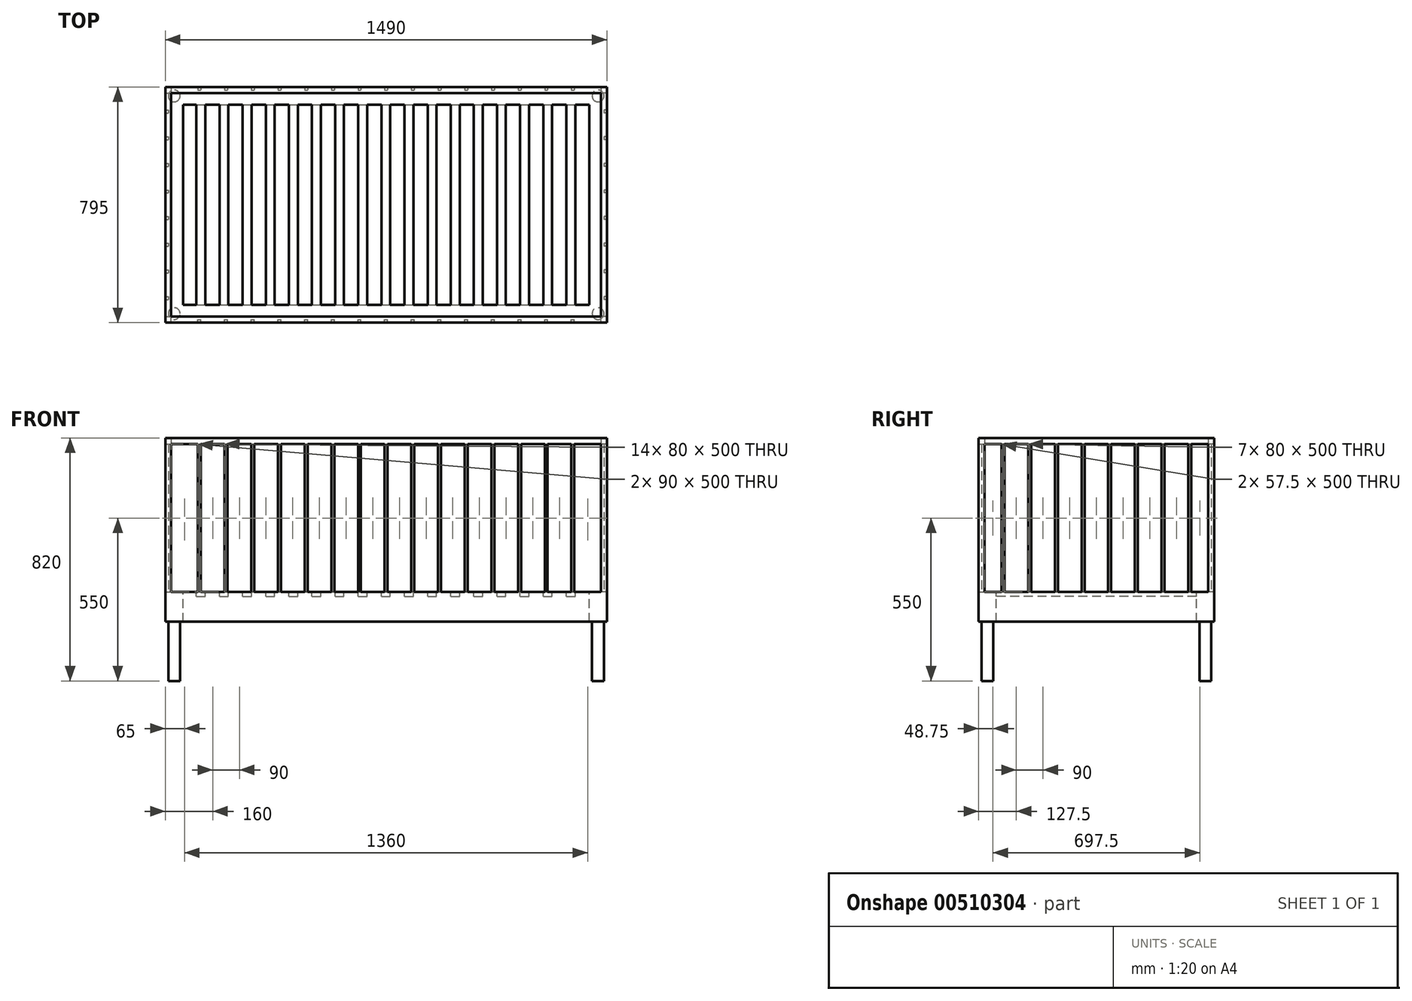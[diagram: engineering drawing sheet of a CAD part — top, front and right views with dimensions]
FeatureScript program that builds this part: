
annotation { "Feature Type Name" : "Feature", "Feature Type Description" : "" }
export const myFeature = defineFeature(function(context is Context, id is Id, definition is map)
    precondition{}
    {
        {
            var Q0;
            Q0=qCreatedBy(makeId("Top.planeOp"),FACE);
            var sketch = newSketch(context, id + "F0", { "sketchPlane" : qUnion([Q0])});
            skLineSegment(sketch, "E0.bottom", {"start": v(-745, 397.5) * mm, "end": v(745, 397.5) * mm});
            skLineSegment(sketch, "E0.top", {"start": v(-745, -397.5) * mm, "end": v(745, -397.5) * mm});
            skLineSegment(sketch, "E0.left", {"start": v(-745, 397.5) * mm, "end": v(-745, -397.5) * mm});
            skLineSegment(sketch, "E0.right", {"start": v(745, 397.5) * mm, "end": v(745, -397.5) * mm});
            skPoint(sketch, "E0.middle", {"position": v(0, 0) * mm});
            skLineSegment(sketch, "E1.bottom", {"start": v(-685, 337.5) * mm, "end": v(685, 337.5) * mm});
            skLineSegment(sketch, "E1.top", {"start": v(-685, -337.5) * mm, "end": v(685, -337.5) * mm});
            skLineSegment(sketch, "E1.left", {"start": v(-685, 337.5) * mm, "end": v(-685, -337.5) * mm});
            skLineSegment(sketch, "E1.right", {"start": v(685, 337.5) * mm, "end": v(685, -337.5) * mm});
            skLineSegment(sketch, "E2", {"start": v(-640, 337.5) * mm, "end": v(-640, -337.5) * mm});
            skLineSegment(sketch, "E3", {"start": v(-640, -337.5) * mm, "end": v(-610, -337.5) * mm});
            skLineSegment(sketch, "E4", {"start": v(-610, -337.5) * mm, "end": v(-610, 337.5) * mm});
            skLineSegment(sketch, "E5.1.0.0", {"start": v(-532, -337.5) * mm, "end": v(-532, 337.5) * mm});
            skLineSegment(sketch, "E5.1.0.1", {"start": v(-562, 337.5) * mm, "end": v(-562, -337.5) * mm});
            skLineSegment(sketch, "E5.2.0.0", {"start": v(-454, -337.5) * mm, "end": v(-454, 337.5) * mm});
            skLineSegment(sketch, "E5.2.0.1", {"start": v(-484, 337.5) * mm, "end": v(-484, -337.5) * mm});
            skLineSegment(sketch, "E5.3.0.0", {"start": v(-376, -337.5) * mm, "end": v(-376, 337.5) * mm});
            skLineSegment(sketch, "E5.3.0.1", {"start": v(-406, 337.5) * mm, "end": v(-406, -337.5) * mm});
            skLineSegment(sketch, "E5.4.0.0", {"start": v(-298, -337.5) * mm, "end": v(-298, 337.5) * mm});
            skLineSegment(sketch, "E5.4.0.1", {"start": v(-328, 337.5) * mm, "end": v(-328, -337.5) * mm});
            skLineSegment(sketch, "E5.5.0.0", {"start": v(-220, -337.5) * mm, "end": v(-220, 337.5) * mm});
            skLineSegment(sketch, "E5.5.0.1", {"start": v(-250, 337.5) * mm, "end": v(-250, -337.5) * mm});
            skLineSegment(sketch, "E5.6.0.0", {"start": v(-142, -337.5) * mm, "end": v(-142, 337.5) * mm});
            skLineSegment(sketch, "E5.6.0.1", {"start": v(-172, 337.5) * mm, "end": v(-172, -337.5) * mm});
            skLineSegment(sketch, "E5.7.0.0", {"start": v(-64, -337.5) * mm, "end": v(-64, 337.5) * mm});
            skLineSegment(sketch, "E5.7.0.1", {"start": v(-94, 337.5) * mm, "end": v(-94, -337.5) * mm});
            skLineSegment(sketch, "E5.8.0.0", {"start": v(14, -337.5) * mm, "end": v(14, 337.5) * mm});
            skLineSegment(sketch, "E5.8.0.1", {"start": v(-16, 337.5) * mm, "end": v(-16, -337.5) * mm});
            skLineSegment(sketch, "E5.9.0.0", {"start": v(92, -337.5) * mm, "end": v(92, 337.5) * mm});
            skLineSegment(sketch, "E5.9.0.1", {"start": v(62, 337.5) * mm, "end": v(62, -337.5) * mm});
            skLineSegment(sketch, "E5.10.0.0", {"start": v(170, -337.5) * mm, "end": v(170, 337.5) * mm});
            skLineSegment(sketch, "E5.10.0.1", {"start": v(140, 337.5) * mm, "end": v(140, -337.5) * mm});
            skLineSegment(sketch, "E5.11.0.0", {"start": v(248, -337.5) * mm, "end": v(248, 337.5) * mm});
            skLineSegment(sketch, "E5.11.0.1", {"start": v(218, 337.5) * mm, "end": v(218, -337.5) * mm});
            skLineSegment(sketch, "E5.12.0.0", {"start": v(326, -337.5) * mm, "end": v(326, 337.5) * mm});
            skLineSegment(sketch, "E5.12.0.1", {"start": v(296, 337.5) * mm, "end": v(296, -337.5) * mm});
            skLineSegment(sketch, "E5.13.0.0", {"start": v(404, -337.5) * mm, "end": v(404, 337.5) * mm});
            skLineSegment(sketch, "E5.13.0.1", {"start": v(374, 337.5) * mm, "end": v(374, -337.5) * mm});
            skLineSegment(sketch, "E5.14.0.0", {"start": v(482, -337.5) * mm, "end": v(482, 337.5) * mm});
            skLineSegment(sketch, "E5.14.0.1", {"start": v(452, 337.5) * mm, "end": v(452, -337.5) * mm});
            skLineSegment(sketch, "E5.15.0.0", {"start": v(560, -337.5) * mm, "end": v(560, 337.5) * mm});
            skLineSegment(sketch, "E5.15.0.1", {"start": v(530, 337.5) * mm, "end": v(530, -337.5) * mm});
            skLineSegment(sketch, "E5.16.0.0", {"start": v(638, -337.5) * mm, "end": v(638, 337.5) * mm});
            skLineSegment(sketch, "E5.16.0.1", {"start": v(608, 337.5) * mm, "end": v(608, -337.5) * mm});
            skLineSegment(sketch, "E5.direction1", {"start": v(-610, -337.5) * mm, "end": v(-532, -337.5) * mm, "construction": true});
            skSolve(sketch);
        }
        {
            var Q0;
            Q0=makeQuery(id+"F0.imprint","IMPRINT",FACE,{"disambiguationData":[TD([[makeQuery(id+"F0.imprint","IMPRINT",EDGE,{"derivedFrom":sQuery(id+"F0.wireOp",EDGE,"E0.bottom")}),-1.0]])]});
            var Q1;
            {var subQ0=sQuery(id+"F0.wireOp",EDGE,"E2");Q1=makeQuery(id+"F0.imprint","IMPRINT",FACE,{"disambiguationData":[TD([[makeQuery(id+"F0.imprint","IMPRINT",EDGE,{"derivedFrom":subQ0}),1.0]])]});}
            var Q2;
            {var subQ0=sQuery(id+"F0.wireOp",EDGE,"E5.1.0.0");Q2=makeQuery(id+"F0.imprint","IMPRINT",FACE,{"disambiguationData":[TD([[makeQuery(id+"F0.imprint","IMPRINT",EDGE,{"derivedFrom":subQ0}),1.0]])]});}
            var Q3;
            {var subQ0=sQuery(id+"F0.wireOp",EDGE,"E5.2.0.0");Q3=makeQuery(id+"F0.imprint","IMPRINT",FACE,{"disambiguationData":[TD([[makeQuery(id+"F0.imprint","IMPRINT",EDGE,{"derivedFrom":subQ0}),1.0]])]});}
            var Q4;
            {var subQ0=sQuery(id+"F0.wireOp",EDGE,"E5.3.0.0");Q4=makeQuery(id+"F0.imprint","IMPRINT",FACE,{"disambiguationData":[TD([[makeQuery(id+"F0.imprint","IMPRINT",EDGE,{"derivedFrom":subQ0}),1.0]])]});}
            var Q5;
            {var subQ0=sQuery(id+"F0.wireOp",EDGE,"E5.4.0.0");Q5=makeQuery(id+"F0.imprint","IMPRINT",FACE,{"disambiguationData":[TD([[makeQuery(id+"F0.imprint","IMPRINT",EDGE,{"derivedFrom":subQ0}),1.0]])]});}
            var Q6;
            {var subQ0=sQuery(id+"F0.wireOp",EDGE,"E5.5.0.0");Q6=makeQuery(id+"F0.imprint","IMPRINT",FACE,{"disambiguationData":[TD([[makeQuery(id+"F0.imprint","IMPRINT",EDGE,{"derivedFrom":subQ0}),1.0]])]});}
            var Q7;
            {var subQ0=sQuery(id+"F0.wireOp",EDGE,"E5.6.0.0");Q7=makeQuery(id+"F0.imprint","IMPRINT",FACE,{"disambiguationData":[TD([[makeQuery(id+"F0.imprint","IMPRINT",EDGE,{"derivedFrom":subQ0}),1.0]])]});}
            var Q8;
            {var subQ0=sQuery(id+"F0.wireOp",EDGE,"E5.7.0.0");Q8=makeQuery(id+"F0.imprint","IMPRINT",FACE,{"disambiguationData":[TD([[makeQuery(id+"F0.imprint","IMPRINT",EDGE,{"derivedFrom":subQ0}),1.0]])]});}
            var Q9;
            {var subQ0=sQuery(id+"F0.wireOp",EDGE,"E5.8.0.0");Q9=makeQuery(id+"F0.imprint","IMPRINT",FACE,{"disambiguationData":[TD([[makeQuery(id+"F0.imprint","IMPRINT",EDGE,{"derivedFrom":subQ0}),1.0]])]});}
            var Q10;
            {var subQ0=sQuery(id+"F0.wireOp",EDGE,"E5.9.0.0");Q10=makeQuery(id+"F0.imprint","IMPRINT",FACE,{"disambiguationData":[TD([[makeQuery(id+"F0.imprint","IMPRINT",EDGE,{"derivedFrom":subQ0}),1.0]])]});}
            var Q11;
            {var subQ0=sQuery(id+"F0.wireOp",EDGE,"E5.10.0.0");Q11=makeQuery(id+"F0.imprint","IMPRINT",FACE,{"disambiguationData":[TD([[makeQuery(id+"F0.imprint","IMPRINT",EDGE,{"derivedFrom":subQ0}),1.0]])]});}
            var Q12;
            {var subQ0=sQuery(id+"F0.wireOp",EDGE,"E5.11.0.0");Q12=makeQuery(id+"F0.imprint","IMPRINT",FACE,{"disambiguationData":[TD([[makeQuery(id+"F0.imprint","IMPRINT",EDGE,{"derivedFrom":subQ0}),1.0]])]});}
            var Q13;
            {var subQ0=sQuery(id+"F0.wireOp",EDGE,"E5.12.0.0");Q13=makeQuery(id+"F0.imprint","IMPRINT",FACE,{"disambiguationData":[TD([[makeQuery(id+"F0.imprint","IMPRINT",EDGE,{"derivedFrom":subQ0}),1.0]])]});}
            var Q14;
            {var subQ0=sQuery(id+"F0.wireOp",EDGE,"E5.13.0.0");Q14=makeQuery(id+"F0.imprint","IMPRINT",FACE,{"disambiguationData":[TD([[makeQuery(id+"F0.imprint","IMPRINT",EDGE,{"derivedFrom":subQ0}),1.0]])]});}
            var Q15;
            {var subQ0=sQuery(id+"F0.wireOp",EDGE,"E5.14.0.0");Q15=makeQuery(id+"F0.imprint","IMPRINT",FACE,{"disambiguationData":[TD([[makeQuery(id+"F0.imprint","IMPRINT",EDGE,{"derivedFrom":subQ0}),1.0]])]});}
            var Q16;
            {var subQ0=sQuery(id+"F0.wireOp",EDGE,"E5.15.0.0");Q16=makeQuery(id+"F0.imprint","IMPRINT",FACE,{"disambiguationData":[TD([[makeQuery(id+"F0.imprint","IMPRINT",EDGE,{"derivedFrom":subQ0}),1.0]])]});}
            var Q17;
            {var subQ0=sQuery(id+"F0.wireOp",EDGE,"E5.16.0.0");Q17=makeQuery(id+"F0.imprint","IMPRINT",FACE,{"disambiguationData":[TD([[makeQuery(id+"F0.imprint","IMPRINT",EDGE,{"derivedFrom":subQ0}),1.0]])]});}
            var Q18;
            {var subQ0=sQuery(id+"F0.wireOp",EDGE,"E5.17.0.0");Q18=makeQuery(id+"F0.imprint","IMPRINT",FACE,{"disambiguationData":[TD([[makeQuery(id+"F0.imprint","IMPRINT",EDGE,{"derivedFrom":subQ0}),1.0]])]});}
            var Q19;
            {var subQ0=sQuery(id+"F0.wireOp",EDGE,"E5.18.0.0");Q19=makeQuery(id+"F0.imprint","IMPRINT",FACE,{"disambiguationData":[TD([[makeQuery(id+"F0.imprint","IMPRINT",EDGE,{"derivedFrom":subQ0}),1.0]])]});}
            var Q20;
            {var subQ0=sQuery(id+"F0.wireOp",EDGE,"E5.19.0.0");Q20=makeQuery(id+"F0.imprint","IMPRINT",FACE,{"disambiguationData":[TD([[makeQuery(id+"F0.imprint","IMPRINT",EDGE,{"derivedFrom":subQ0}),1.0]])]});}
            var Q21;
            {var subQ0=sQuery(id+"F0.wireOp",EDGE,"E5.20.0.0");Q21=makeQuery(id+"F0.imprint","IMPRINT",FACE,{"disambiguationData":[TD([[makeQuery(id+"F0.imprint","IMPRINT",EDGE,{"derivedFrom":subQ0}),1.0]])]});}
            var Q22;
            {var subQ0=sQuery(id+"F0.wireOp",EDGE,"E5.21.0.0");Q22=makeQuery(id+"F0.imprint","IMPRINT",FACE,{"disambiguationData":[TD([[makeQuery(id+"F0.imprint","IMPRINT",EDGE,{"derivedFrom":subQ0}),1.0]])]});}
            var Q23;
            {var subQ0=sQuery(id+"F0.wireOp",EDGE,"E5.22.0.0");Q23=makeQuery(id+"F0.imprint","IMPRINT",FACE,{"disambiguationData":[TD([[makeQuery(id+"F0.imprint","IMPRINT",EDGE,{"derivedFrom":subQ0}),1.0]])]});}
            extrude(context, id + "F1", {"entities" : qUnion([Q0, Q1, Q2, Q3, Q4, Q5, Q6, Q7, Q8, Q9, Q10, Q11, Q12, Q13, Q14, Q15, Q16, Q17, Q18, Q19, Q20, Q21, Q22, Q23]), "oppositeDirection" : true, "depth" : 15 * mm});
        }
        {
            var Q0;
            Q0=qSketchRegion(id+"F0",true);
            extrude(context, id + "F2", {"entities" : qUnion([Q0]), "operationType" : NewBodyOperationType.ADD, "oppositeDirection" : true, "depth" : 100 * mm});
        }
        {
            var Q0;
            Q0=makeQuery(id+"F2.opExtrude","CAP_FACE",FACE,{"disambiguationData":[OSD([sQuery(id+"F0.wireOp",EDGE,"E0.bottom"),sQuery(id+"F0.wireOp",EDGE,"E0.top"),sQuery(id+"F0.wireOp",EDGE,"E0.left"),sQuery(id+"F0.wireOp",EDGE,"E0.right"),sQuery(id+"F0.wireOp",EDGE,"E1.bottom"),sQuery(id+"F0.wireOp",EDGE,"E1.top"),sQuery(id+"F0.wireOp",EDGE,"E1.left"),sQuery(id+"F0.wireOp",EDGE,"E1.right"),sQuery(id+"F0.wireOp",EDGE,"E3")])],"isStart":false});
            var sketch = newSketch(context, id + "F3", { "sketchPlane" : qUnion([Q0])});
            skCircle(sketch, "E6", {"center": v(-715, 367.5) * mm, "radius": 20 * mm});
            skCircle(sketch, "E7", {"center": v(715, 367.5) * mm, "radius": 20 * mm});
            skCircle(sketch, "E8", {"center": v(715, -367.5) * mm, "radius": 20 * mm});
            skCircle(sketch, "E9", {"center": v(-715, -367.5) * mm, "radius": 20 * mm});
            skSolve(sketch);
        }
        {
            var Q0;
            Q0=qSketchRegion(id+"F3",true);
            extrude(context, id + "F4", {"entities" : qUnion([Q0]), "operationType" : NewBodyOperationType.ADD, "depth" : 200 * mm});
        }
        {
            var Q0;
            Q0=makeQuery(id+"F1.opExtrude","CAP_FACE",FACE,{"disambiguationData":[OSD([sQuery(id+"F0.wireOp",EDGE,"E0.bottom"),sQuery(id+"F0.wireOp",EDGE,"E0.top"),sQuery(id+"F0.wireOp",EDGE,"E0.left"),sQuery(id+"F0.wireOp",EDGE,"E0.right"),sQuery(id+"F0.wireOp",EDGE,"E1.bottom"),sQuery(id+"F0.wireOp",EDGE,"E1.top"),sQuery(id+"F0.wireOp",EDGE,"E1.left"),sQuery(id+"F0.wireOp",EDGE,"E1.right"),sQuery(id+"F0.wireOp",EDGE,"E2"),sQuery(id+"F0.wireOp",EDGE,"E4"),sQuery(id+"F0.wireOp",EDGE,"E5.1.0.0"),sQuery(id+"F0.wireOp",EDGE,"E5.1.0.1"),sQuery(id+"F0.wireOp",EDGE,"E5.2.0.0"),sQuery(id+"F0.wireOp",EDGE,"E5.2.0.1"),sQuery(id+"F0.wireOp",EDGE,"E5.3.0.0"),sQuery(id+"F0.wireOp",EDGE,"E5.3.0.1"),sQuery(id+"F0.wireOp",EDGE,"E5.4.0.0"),sQuery(id+"F0.wireOp",EDGE,"E5.4.0.1"),sQuery(id+"F0.wireOp",EDGE,"E5.5.0.0"),sQuery(id+"F0.wireOp",EDGE,"E5.5.0.1"),sQuery(id+"F0.wireOp",EDGE,"E5.6.0.0"),sQuery(id+"F0.wireOp",EDGE,"E5.6.0.1"),sQuery(id+"F0.wireOp",EDGE,"E5.7.0.0"),sQuery(id+"F0.wireOp",EDGE,"E5.7.0.1"),sQuery(id+"F0.wireOp",EDGE,"E5.8.0.0"),sQuery(id+"F0.wireOp",EDGE,"E5.8.0.1"),sQuery(id+"F0.wireOp",EDGE,"E5.9.0.0"),sQuery(id+"F0.wireOp",EDGE,"E5.9.0.1"),sQuery(id+"F0.wireOp",EDGE,"E5.10.0.0"),sQuery(id+"F0.wireOp",EDGE,"E5.10.0.1"),sQuery(id+"F0.wireOp",EDGE,"E5.11.0.0"),sQuery(id+"F0.wireOp",EDGE,"E5.11.0.1"),sQuery(id+"F0.wireOp",EDGE,"E5.12.0.0"),sQuery(id+"F0.wireOp",EDGE,"E5.12.0.1"),sQuery(id+"F0.wireOp",EDGE,"E5.13.0.0"),sQuery(id+"F0.wireOp",EDGE,"E5.13.0.1"),sQuery(id+"F0.wireOp",EDGE,"E5.14.0.0"),sQuery(id+"F0.wireOp",EDGE,"E5.14.0.1"),sQuery(id+"F0.wireOp",EDGE,"E5.15.0.0"),sQuery(id+"F0.wireOp",EDGE,"E5.15.0.1"),sQuery(id+"F0.wireOp",EDGE,"E5.16.0.0"),sQuery(id+"F0.wireOp",EDGE,"E5.16.0.1")])],"isStart":true});
            var sketch = newSketch(context, id + "F5", { "sketchPlane" : qUnion([Q0])});
            skLineSegment(sketch, "E10.bottom", {"start": v(-745, 397.5) * mm, "end": v(-725, 397.5) * mm});
            skLineSegment(sketch, "E10.top", {"start": v(-745, 377.5) * mm, "end": v(-725, 377.5) * mm});
            skLineSegment(sketch, "E10.left", {"start": v(-745, 397.5) * mm, "end": v(-745, 377.5) * mm});
            skLineSegment(sketch, "E10.right", {"start": v(-725, 397.5) * mm, "end": v(-725, 377.5) * mm});
            skLineSegment(sketch, "E11.bottom", {"start": v(745, 397.5) * mm, "end": v(725, 397.5) * mm});
            skLineSegment(sketch, "E11.top", {"start": v(745, 377.5) * mm, "end": v(725, 377.5) * mm});
            skLineSegment(sketch, "E11.left", {"start": v(745, 397.5) * mm, "end": v(745, 377.5) * mm});
            skLineSegment(sketch, "E11.right", {"start": v(725, 397.5) * mm, "end": v(725, 377.5) * mm});
            skLineSegment(sketch, "E12.bottom", {"start": v(-635, 397.5) * mm, "end": v(-625, 397.5) * mm});
            skLineSegment(sketch, "E12.top", {"start": v(-635, 387.5) * mm, "end": v(-625, 387.5) * mm});
            skLineSegment(sketch, "E12.left", {"start": v(-635, 397.5) * mm, "end": v(-635, 387.5) * mm});
            skLineSegment(sketch, "E12.right", {"start": v(-625, 397.5) * mm, "end": v(-625, 387.5) * mm});
            skLineSegment(sketch, "E13.1.0.0", {"start": v(-545, 387.5) * mm, "end": v(-535, 387.5) * mm});
            skLineSegment(sketch, "E13.1.0.1", {"start": v(-545, 397.5) * mm, "end": v(-535, 397.5) * mm});
            skLineSegment(sketch, "E13.1.0.2", {"start": v(-535, 397.5) * mm, "end": v(-535, 387.5) * mm});
            skLineSegment(sketch, "E13.1.0.3", {"start": v(-545, 397.5) * mm, "end": v(-545, 387.5) * mm});
            skLineSegment(sketch, "E13.2.0.0", {"start": v(-455, 387.5) * mm, "end": v(-445, 387.5) * mm});
            skLineSegment(sketch, "E13.2.0.1", {"start": v(-455, 397.5) * mm, "end": v(-445, 397.5) * mm});
            skLineSegment(sketch, "E13.2.0.2", {"start": v(-445, 397.5) * mm, "end": v(-445, 387.5) * mm});
            skLineSegment(sketch, "E13.2.0.3", {"start": v(-455, 397.5) * mm, "end": v(-455, 387.5) * mm});
            skLineSegment(sketch, "E13.3.0.0", {"start": v(-365, 387.5) * mm, "end": v(-355, 387.5) * mm});
            skLineSegment(sketch, "E13.3.0.1", {"start": v(-365, 397.5) * mm, "end": v(-355, 397.5) * mm});
            skLineSegment(sketch, "E13.3.0.2", {"start": v(-355, 397.5) * mm, "end": v(-355, 387.5) * mm});
            skLineSegment(sketch, "E13.3.0.3", {"start": v(-365, 397.5) * mm, "end": v(-365, 387.5) * mm});
            skLineSegment(sketch, "E13.4.0.0", {"start": v(-275, 387.5) * mm, "end": v(-265, 387.5) * mm});
            skLineSegment(sketch, "E13.4.0.1", {"start": v(-275, 397.5) * mm, "end": v(-265, 397.5) * mm});
            skLineSegment(sketch, "E13.4.0.2", {"start": v(-265, 397.5) * mm, "end": v(-265, 387.5) * mm});
            skLineSegment(sketch, "E13.4.0.3", {"start": v(-275, 397.5) * mm, "end": v(-275, 387.5) * mm});
            skLineSegment(sketch, "E13.5.0.0", {"start": v(-185, 387.5) * mm, "end": v(-175, 387.5) * mm});
            skLineSegment(sketch, "E13.5.0.1", {"start": v(-185, 397.5) * mm, "end": v(-175, 397.5) * mm});
            skLineSegment(sketch, "E13.5.0.2", {"start": v(-175, 397.5) * mm, "end": v(-175, 387.5) * mm});
            skLineSegment(sketch, "E13.5.0.3", {"start": v(-185, 397.5) * mm, "end": v(-185, 387.5) * mm});
            skLineSegment(sketch, "E13.6.0.0", {"start": v(-95, 387.5) * mm, "end": v(-85, 387.5) * mm});
            skLineSegment(sketch, "E13.6.0.1", {"start": v(-95, 397.5) * mm, "end": v(-85, 397.5) * mm});
            skLineSegment(sketch, "E13.6.0.2", {"start": v(-85, 397.5) * mm, "end": v(-85, 387.5) * mm});
            skLineSegment(sketch, "E13.6.0.3", {"start": v(-95, 397.5) * mm, "end": v(-95, 387.5) * mm});
            skLineSegment(sketch, "E13.7.0.0", {"start": v(-5, 387.5) * mm, "end": v(5, 387.5) * mm});
            skLineSegment(sketch, "E13.7.0.1", {"start": v(-5, 397.5) * mm, "end": v(5, 397.5) * mm});
            skLineSegment(sketch, "E13.7.0.2", {"start": v(5, 397.5) * mm, "end": v(5, 387.5) * mm});
            skLineSegment(sketch, "E13.7.0.3", {"start": v(-5, 397.5) * mm, "end": v(-5, 387.5) * mm});
            skLineSegment(sketch, "E13.8.0.0", {"start": v(85, 387.5) * mm, "end": v(95, 387.5) * mm});
            skLineSegment(sketch, "E13.8.0.1", {"start": v(85, 397.5) * mm, "end": v(95, 397.5) * mm});
            skLineSegment(sketch, "E13.8.0.2", {"start": v(95, 397.5) * mm, "end": v(95, 387.5) * mm});
            skLineSegment(sketch, "E13.8.0.3", {"start": v(85, 397.5) * mm, "end": v(85, 387.5) * mm});
            skLineSegment(sketch, "E13.9.0.0", {"start": v(175, 387.5) * mm, "end": v(185, 387.5) * mm});
            skLineSegment(sketch, "E13.9.0.1", {"start": v(175, 397.5) * mm, "end": v(185, 397.5) * mm});
            skLineSegment(sketch, "E13.9.0.2", {"start": v(185, 397.5) * mm, "end": v(185, 387.5) * mm});
            skLineSegment(sketch, "E13.9.0.3", {"start": v(175, 397.5) * mm, "end": v(175, 387.5) * mm});
            skLineSegment(sketch, "E13.10.0.0", {"start": v(265, 387.5) * mm, "end": v(275, 387.5) * mm});
            skLineSegment(sketch, "E13.10.0.1", {"start": v(265, 397.5) * mm, "end": v(275, 397.5) * mm});
            skLineSegment(sketch, "E13.10.0.2", {"start": v(275, 397.5) * mm, "end": v(275, 387.5) * mm});
            skLineSegment(sketch, "E13.10.0.3", {"start": v(265, 397.5) * mm, "end": v(265, 387.5) * mm});
            skLineSegment(sketch, "E13.11.0.0", {"start": v(355, 387.5) * mm, "end": v(365, 387.5) * mm});
            skLineSegment(sketch, "E13.11.0.1", {"start": v(355, 397.5) * mm, "end": v(365, 397.5) * mm});
            skLineSegment(sketch, "E13.11.0.2", {"start": v(365, 397.5) * mm, "end": v(365, 387.5) * mm});
            skLineSegment(sketch, "E13.11.0.3", {"start": v(355, 397.5) * mm, "end": v(355, 387.5) * mm});
            skLineSegment(sketch, "E13.12.0.0", {"start": v(445, 387.5) * mm, "end": v(455, 387.5) * mm});
            skLineSegment(sketch, "E13.12.0.1", {"start": v(445, 397.5) * mm, "end": v(455, 397.5) * mm});
            skLineSegment(sketch, "E13.12.0.2", {"start": v(455, 397.5) * mm, "end": v(455, 387.5) * mm});
            skLineSegment(sketch, "E13.12.0.3", {"start": v(445, 397.5) * mm, "end": v(445, 387.5) * mm});
            skLineSegment(sketch, "E13.13.0.0", {"start": v(535, 387.5) * mm, "end": v(545, 387.5) * mm});
            skLineSegment(sketch, "E13.13.0.1", {"start": v(535, 397.5) * mm, "end": v(545, 397.5) * mm});
            skLineSegment(sketch, "E13.13.0.2", {"start": v(545, 397.5) * mm, "end": v(545, 387.5) * mm});
            skLineSegment(sketch, "E13.13.0.3", {"start": v(535, 397.5) * mm, "end": v(535, 387.5) * mm});
            skLineSegment(sketch, "E13.14.0.0", {"start": v(625, 387.5) * mm, "end": v(635, 387.5) * mm});
            skLineSegment(sketch, "E13.14.0.1", {"start": v(625, 397.5) * mm, "end": v(635, 397.5) * mm});
            skLineSegment(sketch, "E13.14.0.2", {"start": v(635, 397.5) * mm, "end": v(635, 387.5) * mm});
            skLineSegment(sketch, "E13.14.0.3", {"start": v(625, 397.5) * mm, "end": v(625, 387.5) * mm});
            skLineSegment(sketch, "E13.direction1", {"start": v(-635, 387.5) * mm, "end": v(-545, 387.5) * mm, "construction": true});
            skLineSegment(sketch, "E14.MirrorCS", {"start": v(-635, -387.5) * mm, "end": v(-625, -387.5) * mm});
            skLineSegment(sketch, "E15.MirrorCS", {"start": v(-635, -397.5) * mm, "end": v(-625, -397.5) * mm});
            skLineSegment(sketch, "E16.MirrorCS", {"start": v(-545, -397.5) * mm, "end": v(-535, -397.5) * mm});
            skLineSegment(sketch, "E17.MirrorCS", {"start": v(625, -397.5) * mm, "end": v(635, -397.5) * mm});
            skLineSegment(sketch, "E18.MirrorCS", {"start": v(625, -387.5) * mm, "end": v(635, -387.5) * mm});
            skLineSegment(sketch, "E19.MirrorCS", {"start": v(-545, -387.5) * mm, "end": v(-535, -387.5) * mm});
            skLineSegment(sketch, "E20.MirrorCS", {"start": v(-625, -397.5) * mm, "end": v(-625, -387.5) * mm});
            skLineSegment(sketch, "E21.MirrorCS", {"start": v(-635, -397.5) * mm, "end": v(-635, -387.5) * mm});
            skLineSegment(sketch, "E22.MirrorCS", {"start": v(-725, -397.5) * mm, "end": v(-725, -377.5) * mm});
            skLineSegment(sketch, "E23.MirrorCS", {"start": v(-745, -397.5) * mm, "end": v(-725, -397.5) * mm});
            skLineSegment(sketch, "E24.MirrorCS", {"start": v(-545, -397.5) * mm, "end": v(-545, -387.5) * mm});
            skLineSegment(sketch, "E25.MirrorCS", {"start": v(-535, -397.5) * mm, "end": v(-535, -387.5) * mm});
            skLineSegment(sketch, "E26.MirrorCS", {"start": v(85, -397.5) * mm, "end": v(95, -397.5) * mm});
            skLineSegment(sketch, "E27.MirrorCS", {"start": v(535, -397.5) * mm, "end": v(545, -397.5) * mm});
            skLineSegment(sketch, "E28.MirrorCS", {"start": v(-455, -387.5) * mm, "end": v(-445, -387.5) * mm});
            skLineSegment(sketch, "E29.MirrorCS", {"start": v(175, -387.5) * mm, "end": v(185, -387.5) * mm});
            skLineSegment(sketch, "E30.MirrorCS", {"start": v(535, -387.5) * mm, "end": v(545, -387.5) * mm});
            skLineSegment(sketch, "E31.MirrorCS", {"start": v(175, -397.5) * mm, "end": v(185, -397.5) * mm});
            skLineSegment(sketch, "E32.MirrorCS", {"start": v(-455, -397.5) * mm, "end": v(-445, -397.5) * mm});
            skLineSegment(sketch, "E33.MirrorCS", {"start": v(635, -397.5) * mm, "end": v(635, -387.5) * mm});
            skLineSegment(sketch, "E34.MirrorCS", {"start": v(85, -387.5) * mm, "end": v(95, -387.5) * mm});
            skLineSegment(sketch, "E35.MirrorCS", {"start": v(625, -397.5) * mm, "end": v(625, -387.5) * mm});
            skLineSegment(sketch, "E36.MirrorCS", {"start": v(725, -397.5) * mm, "end": v(725, -377.5) * mm});
            skLineSegment(sketch, "E37.MirrorCS", {"start": v(745, -397.5) * mm, "end": v(745, -377.5) * mm});
            skLineSegment(sketch, "E38.MirrorCS", {"start": v(745, -377.5) * mm, "end": v(725, -377.5) * mm});
            skLineSegment(sketch, "E39.MirrorCS", {"start": v(-355, -397.5) * mm, "end": v(-355, -387.5) * mm});
            skLineSegment(sketch, "E40.MirrorCS", {"start": v(5, -397.5) * mm, "end": v(5, -387.5) * mm});
            skLineSegment(sketch, "E41.MirrorCS", {"start": v(-185, -397.5) * mm, "end": v(-185, -387.5) * mm});
            skLineSegment(sketch, "E42.MirrorCS", {"start": v(175, -397.5) * mm, "end": v(175, -387.5) * mm});
            skLineSegment(sketch, "E43.MirrorCS", {"start": v(365, -397.5) * mm, "end": v(365, -387.5) * mm});
            skLineSegment(sketch, "E44.MirrorCS", {"start": v(535, -397.5) * mm, "end": v(535, -387.5) * mm});
            skLineSegment(sketch, "E45.MirrorCS", {"start": v(745, -397.5) * mm, "end": v(725, -397.5) * mm});
            skLineSegment(sketch, "E46.MirrorCS", {"start": v(-745, -397.5) * mm, "end": v(-745, -377.5) * mm});
            skLineSegment(sketch, "E47.MirrorCS", {"start": v(-745, -377.5) * mm, "end": v(-725, -377.5) * mm});
            skLineSegment(sketch, "E48.MirrorCS", {"start": v(-365, -397.5) * mm, "end": v(-365, -387.5) * mm});
            skLineSegment(sketch, "E49.MirrorCS", {"start": v(-275, -397.5) * mm, "end": v(-275, -387.5) * mm});
            skLineSegment(sketch, "E50.MirrorCS", {"start": v(-95, -397.5) * mm, "end": v(-85, -397.5) * mm});
            skLineSegment(sketch, "E51.MirrorCS", {"start": v(355, -397.5) * mm, "end": v(365, -397.5) * mm});
            skLineSegment(sketch, "E52.MirrorCS", {"start": v(-95, -397.5) * mm, "end": v(-95, -387.5) * mm});
            skLineSegment(sketch, "E53.MirrorCS", {"start": v(-365, -397.5) * mm, "end": v(-355, -397.5) * mm});
            skLineSegment(sketch, "E54.MirrorCS", {"start": v(265, -397.5) * mm, "end": v(275, -397.5) * mm});
            skLineSegment(sketch, "E55.MirrorCS", {"start": v(95, -397.5) * mm, "end": v(95, -387.5) * mm});
            skLineSegment(sketch, "E56.MirrorCS", {"start": v(455, -397.5) * mm, "end": v(455, -387.5) * mm});
            skLineSegment(sketch, "E57.MirrorCS", {"start": v(265, -397.5) * mm, "end": v(265, -387.5) * mm});
            skLineSegment(sketch, "E58.MirrorCS", {"start": v(445, -397.5) * mm, "end": v(455, -397.5) * mm});
            skLineSegment(sketch, "E59.MirrorCS", {"start": v(265, -387.5) * mm, "end": v(275, -387.5) * mm});
            skLineSegment(sketch, "E60.MirrorCS", {"start": v(-85, -397.5) * mm, "end": v(-85, -387.5) * mm});
            skLineSegment(sketch, "E61.MirrorCS", {"start": v(355, -387.5) * mm, "end": v(365, -387.5) * mm});
            skLineSegment(sketch, "E62.MirrorCS", {"start": v(275, -397.5) * mm, "end": v(275, -387.5) * mm});
            skLineSegment(sketch, "E63.MirrorCS", {"start": v(355, -397.5) * mm, "end": v(355, -387.5) * mm});
            skLineSegment(sketch, "E64.MirrorCS", {"start": v(-365, -387.5) * mm, "end": v(-355, -387.5) * mm});
            skLineSegment(sketch, "E65.MirrorCS", {"start": v(-5, -387.5) * mm, "end": v(5, -387.5) * mm});
            skLineSegment(sketch, "E66.MirrorCS", {"start": v(-455, -397.5) * mm, "end": v(-455, -387.5) * mm});
            skLineSegment(sketch, "E67.MirrorCS", {"start": v(-445, -397.5) * mm, "end": v(-445, -387.5) * mm});
            skLineSegment(sketch, "E68.MirrorCS", {"start": v(-95, -387.5) * mm, "end": v(-85, -387.5) * mm});
            skLineSegment(sketch, "E69.MirrorCS", {"start": v(445, -397.5) * mm, "end": v(445, -387.5) * mm});
            skLineSegment(sketch, "E70.MirrorCS", {"start": v(-265, -397.5) * mm, "end": v(-265, -387.5) * mm});
            skLineSegment(sketch, "E71.MirrorCS", {"start": v(85, -397.5) * mm, "end": v(85, -387.5) * mm});
            skLineSegment(sketch, "E72.MirrorCS", {"start": v(-185, -397.5) * mm, "end": v(-175, -397.5) * mm});
            skLineSegment(sketch, "E73.MirrorCS", {"start": v(-275, -397.5) * mm, "end": v(-265, -397.5) * mm});
            skLineSegment(sketch, "E74.MirrorCS", {"start": v(-185, -387.5) * mm, "end": v(-175, -387.5) * mm});
            skLineSegment(sketch, "E75.MirrorCS", {"start": v(185, -397.5) * mm, "end": v(185, -387.5) * mm});
            skLineSegment(sketch, "E76.MirrorCS", {"start": v(-5, -397.5) * mm, "end": v(5, -397.5) * mm});
            skLineSegment(sketch, "E77.MirrorCS", {"start": v(545, -397.5) * mm, "end": v(545, -387.5) * mm});
            skLineSegment(sketch, "E78.MirrorCS", {"start": v(-275, -387.5) * mm, "end": v(-265, -387.5) * mm});
            skLineSegment(sketch, "E79.MirrorCS", {"start": v(445, -387.5) * mm, "end": v(455, -387.5) * mm});
            skLineSegment(sketch, "E80.MirrorCS", {"start": v(-175, -397.5) * mm, "end": v(-175, -387.5) * mm});
            skLineSegment(sketch, "E81.MirrorCS", {"start": v(-5, -397.5) * mm, "end": v(-5, -387.5) * mm});
            skLineSegment(sketch, "E82.MirrorCS", {"start": v(-635, -387.5) * mm, "end": v(-545, -387.5) * mm, "construction": true});
            skLineSegment(sketch, "E83.bottom", {"start": v(-745, 320) * mm, "end": v(-735, 320) * mm});
            skLineSegment(sketch, "E83.top", {"start": v(-745, 310) * mm, "end": v(-735, 310) * mm});
            skLineSegment(sketch, "E83.left", {"start": v(-745, 320) * mm, "end": v(-745, 310) * mm});
            skLineSegment(sketch, "E83.right", {"start": v(-735, 320) * mm, "end": v(-735, 310) * mm});
            skLineSegment(sketch, "E84.0.1.0", {"start": v(-745, 220) * mm, "end": v(-735, 220) * mm});
            skLineSegment(sketch, "E84.0.1.1", {"start": v(-745, 230) * mm, "end": v(-745, 220) * mm});
            skLineSegment(sketch, "E84.0.1.2", {"start": v(-745, 230) * mm, "end": v(-735, 230) * mm});
            skLineSegment(sketch, "E84.0.1.3", {"start": v(-735, 230) * mm, "end": v(-735, 220) * mm});
            skLineSegment(sketch, "E84.0.2.0", {"start": v(-745, 130) * mm, "end": v(-735, 130) * mm});
            skLineSegment(sketch, "E84.0.2.1", {"start": v(-745, 140) * mm, "end": v(-745, 130) * mm});
            skLineSegment(sketch, "E84.0.2.2", {"start": v(-745, 140) * mm, "end": v(-735, 140) * mm});
            skLineSegment(sketch, "E84.0.2.3", {"start": v(-735, 140) * mm, "end": v(-735, 130) * mm});
            skLineSegment(sketch, "E84.0.3.0", {"start": v(-745, 40) * mm, "end": v(-735, 40) * mm});
            skLineSegment(sketch, "E84.0.3.1", {"start": v(-745, 50) * mm, "end": v(-745, 40) * mm});
            skLineSegment(sketch, "E84.0.3.2", {"start": v(-745, 50) * mm, "end": v(-735, 50) * mm});
            skLineSegment(sketch, "E84.0.3.3", {"start": v(-735, 50) * mm, "end": v(-735, 40) * mm});
            skLineSegment(sketch, "E84.0.4.0", {"start": v(-745, -50) * mm, "end": v(-735, -50) * mm});
            skLineSegment(sketch, "E84.0.4.1", {"start": v(-745, -40) * mm, "end": v(-745, -50) * mm});
            skLineSegment(sketch, "E84.0.4.2", {"start": v(-745, -40) * mm, "end": v(-735, -40) * mm});
            skLineSegment(sketch, "E84.0.4.3", {"start": v(-735, -40) * mm, "end": v(-735, -50) * mm});
            skLineSegment(sketch, "E84.0.5.0", {"start": v(-745, -140) * mm, "end": v(-735, -140) * mm});
            skLineSegment(sketch, "E84.0.5.1", {"start": v(-745, -130) * mm, "end": v(-745, -140) * mm});
            skLineSegment(sketch, "E84.0.5.2", {"start": v(-745, -130) * mm, "end": v(-735, -130) * mm});
            skLineSegment(sketch, "E84.0.5.3", {"start": v(-735, -130) * mm, "end": v(-735, -140) * mm});
            skLineSegment(sketch, "E84.0.6.0", {"start": v(-745, -230) * mm, "end": v(-735, -230) * mm});
            skLineSegment(sketch, "E84.0.6.1", {"start": v(-745, -220) * mm, "end": v(-745, -230) * mm});
            skLineSegment(sketch, "E84.0.6.2", {"start": v(-745, -220) * mm, "end": v(-735, -220) * mm});
            skLineSegment(sketch, "E84.0.6.3", {"start": v(-735, -220) * mm, "end": v(-735, -230) * mm});
            skLineSegment(sketch, "E84.0.7.0", {"start": v(-745, -320) * mm, "end": v(-735, -320) * mm});
            skLineSegment(sketch, "E84.0.7.1", {"start": v(-745, -310) * mm, "end": v(-745, -320) * mm});
            skLineSegment(sketch, "E84.0.7.2", {"start": v(-745, -310) * mm, "end": v(-735, -310) * mm});
            skLineSegment(sketch, "E84.0.7.3", {"start": v(-735, -310) * mm, "end": v(-735, -320) * mm});
            skLineSegment(sketch, "E84.direction1", {"start": v(-745, 310) * mm, "end": v(-720, 310) * mm, "construction": true});
            skLineSegment(sketch, "E84.direction2", {"start": v(-745, 310) * mm, "end": v(-745, 220) * mm, "construction": true});
            skLineSegment(sketch, "E85.MirrorCS", {"start": v(745, 310) * mm, "end": v(735, 310) * mm});
            skLineSegment(sketch, "E86.MirrorCS", {"start": v(745, 230) * mm, "end": v(735, 230) * mm});
            skLineSegment(sketch, "E87.MirrorCS", {"start": v(745, 320) * mm, "end": v(745, 310) * mm});
            skLineSegment(sketch, "E88.MirrorCS", {"start": v(735, 320) * mm, "end": v(735, 310) * mm});
            skLineSegment(sketch, "E89.MirrorCS", {"start": v(745, 320) * mm, "end": v(735, 320) * mm});
            skLineSegment(sketch, "E90.MirrorCS", {"start": v(745, 310) * mm, "end": v(720, 310) * mm, "construction": true});
            skLineSegment(sketch, "E91.MirrorCS", {"start": v(745, -130) * mm, "end": v(735, -130) * mm});
            skLineSegment(sketch, "E92.MirrorCS", {"start": v(735, 230) * mm, "end": v(735, 220) * mm});
            skLineSegment(sketch, "E93.MirrorCS", {"start": v(745, -230) * mm, "end": v(735, -230) * mm});
            skLineSegment(sketch, "E94.MirrorCS", {"start": v(745, 230) * mm, "end": v(745, 220) * mm});
            skLineSegment(sketch, "E95.MirrorCS", {"start": v(745, 220) * mm, "end": v(735, 220) * mm});
            skLineSegment(sketch, "E96.MirrorCS", {"start": v(745, -320) * mm, "end": v(735, -320) * mm});
            skLineSegment(sketch, "E97.MirrorCS", {"start": v(745, 40) * mm, "end": v(735, 40) * mm});
            skLineSegment(sketch, "E98.MirrorCS", {"start": v(735, -130) * mm, "end": v(735, -140) * mm});
            skLineSegment(sketch, "E99.MirrorCS", {"start": v(745, 130) * mm, "end": v(735, 130) * mm});
            skLineSegment(sketch, "E100.MirrorCS", {"start": v(745, -130) * mm, "end": v(745, -140) * mm});
            skLineSegment(sketch, "E101.MirrorCS", {"start": v(745, -140) * mm, "end": v(735, -140) * mm});
            skLineSegment(sketch, "E102.MirrorCS", {"start": v(745, -40) * mm, "end": v(735, -40) * mm});
            skLineSegment(sketch, "E103.MirrorCS", {"start": v(735, -40) * mm, "end": v(735, -50) * mm});
            skLineSegment(sketch, "E104.MirrorCS", {"start": v(745, -40) * mm, "end": v(745, -50) * mm});
            skLineSegment(sketch, "E105.MirrorCS", {"start": v(745, -50) * mm, "end": v(735, -50) * mm});
            skLineSegment(sketch, "E106.MirrorCS", {"start": v(735, 50) * mm, "end": v(735, 40) * mm});
            skLineSegment(sketch, "E107.MirrorCS", {"start": v(735, -310) * mm, "end": v(735, -320) * mm});
            skLineSegment(sketch, "E108.MirrorCS", {"start": v(745, -220) * mm, "end": v(745, -230) * mm});
            skLineSegment(sketch, "E109.MirrorCS", {"start": v(745, 140) * mm, "end": v(745, 130) * mm});
            skLineSegment(sketch, "E110.MirrorCS", {"start": v(735, -220) * mm, "end": v(735, -230) * mm});
            skLineSegment(sketch, "E111.MirrorCS", {"start": v(735, 140) * mm, "end": v(735, 130) * mm});
            skLineSegment(sketch, "E112.MirrorCS", {"start": v(745, -220) * mm, "end": v(735, -220) * mm});
            skLineSegment(sketch, "E113.MirrorCS", {"start": v(745, 50) * mm, "end": v(735, 50) * mm});
            skLineSegment(sketch, "E114.MirrorCS", {"start": v(745, -310) * mm, "end": v(735, -310) * mm});
            skLineSegment(sketch, "E115.MirrorCS", {"start": v(745, 50) * mm, "end": v(745, 40) * mm});
            skLineSegment(sketch, "E116.MirrorCS", {"start": v(745, 140) * mm, "end": v(735, 140) * mm});
            skLineSegment(sketch, "E117.MirrorCS", {"start": v(745, -310) * mm, "end": v(745, -320) * mm});
            skLineSegment(sketch, "E118.MirrorCS", {"start": v(745, 310) * mm, "end": v(745, 220) * mm, "construction": true});
            skSolve(sketch);
        }
        {
            var Q0;
            Q0=qSketchRegion(id+"F5",true);
            extrude(context, id + "F6", {"entities" : qUnion([Q0]), "operationType" : NewBodyOperationType.ADD, "depth" : 500 * mm});
        }
        {
            var Q0;
            Q0=makeQuery(id+"F6.opExtrude","CAP_FACE",FACE,{"disambiguationData":[OSD([sQuery(id+"F5.wireOp",EDGE,"E10.bottom"),sQuery(id+"F5.wireOp",EDGE,"E10.top"),sQuery(id+"F5.wireOp",EDGE,"E10.left"),sQuery(id+"F5.wireOp",EDGE,"E10.right")])],"isStart":false});
            var sketch = newSketch(context, id + "F7", { "sketchPlane" : qUnion([Q0])});
            skLineSegment(sketch, "E119.bottom", {"start": v(-745, 397.5) * mm, "end": v(745, 397.5) * mm});
            skLineSegment(sketch, "E119.top", {"start": v(-725, 377.5) * mm, "end": v(725, 377.5) * mm});
            skLineSegment(sketch, "E119.left", {"start": v(-745, 397.5) * mm, "end": v(-745, 377.5) * mm});
            skLineSegment(sketch, "E119.right", {"start": v(745, 397.5) * mm, "end": v(745, 377.5) * mm});
            skLineSegment(sketch, "E120.bottom", {"start": v(-745, 397.5) * mm, "end": v(-725, 397.5) * mm});
            skLineSegment(sketch, "E120.top", {"start": v(-745, -397.5) * mm, "end": v(-725, -397.5) * mm});
            skLineSegment(sketch, "E120.left", {"start": v(-745, 397.5) * mm, "end": v(-745, -397.5) * mm});
            skLineSegment(sketch, "E120.right", {"start": v(-725, 377.5) * mm, "end": v(-725, -377.5) * mm});
            skLineSegment(sketch, "E121.MirrorCS", {"start": v(-725, -377.5) * mm, "end": v(725, -377.5) * mm});
            skLineSegment(sketch, "E122.MirrorCS", {"start": v(-745, -397.5) * mm, "end": v(745, -397.5) * mm});
            skLineSegment(sketch, "E123.MirrorCS", {"start": v(725, 377.5) * mm, "end": v(725, -377.5) * mm});
            skLineSegment(sketch, "E124.MirrorCS", {"start": v(745, 397.5) * mm, "end": v(745, -397.5) * mm});
            skPoint(sketch, "E125.orphan", {"position": v(725, 397.5) * mm});
            skPoint(sketch, "E126.orphan", {"position": v(745, -377.5) * mm});
            skPoint(sketch, "E127.orphan", {"position": v(725, -397.5) * mm});
            skPoint(sketch, "E128.orphan", {"position": v(-745, -377.5) * mm});
            skSolve(sketch);
        }
        {
            var Q0;
            Q0=qSketchRegion(id+"F7",true);
            extrude(context, id + "F8", {"entities" : qUnion([Q0]), "operationType" : NewBodyOperationType.ADD, "depth" : 20 * mm});
        }
    });
